# Revit family: Caroma TMV20 Bottom Inlet Hinged
name_source: partatom
category: Pipe Accessories
revit_build: Autodesk Revit LT 2014 (Build: 20130308_1515(x64)
units: mm (PartAtom-declared; Revit-internal decimal feet)

## types (2) — shared parameters
Assembly Code = D2090800
Description = Thermostatic Mixing Valve in Stainless Steel Enclosure (Hinged Door)
Height_ANZRS = 320 mm  [stored 1.04987 ft]
Length_ANZRS = 320 mm  [stored 1.04987 ft]
Manufacturer = GWA Bathrooms & Kitchens
Material_ANZRS = Metal-Stainless Steel-Brushed
ModifiedIssue_ANZRS = 20150421.04 $
PlumbingMaterial_ANZRS = Metal-Copper-Satin
Side2Flow_ANZRS = 0.7 L/s
Type Comments = Adjustable Temperature range 35-50°, Dynamic Working Pressure 20-500kPa, Maximum 1000kPa Inlet Pressure, Maximum Ratio 10:1
URL = http://specify.caroma.com.au
Width_ANZRS = 75 mm  [stored 0.246063 ft]
zero-valued in all types: K Coefficient

## per-type parameters (varying)
| type | Angle | End1 pos | End2 Pos | Model | Top Inlet |
| Bottom Inlet | 90.00° | 411 mm  [stored 1.34843 ft] | 522 mm | BTMV20-005 | No |
| Top Inlet | 270.00° | 111 mm | 0 mm  [stored 0 ft] | BTMV20-006 | Yes |

note: [stored X ft] marks values corroborated as IEEE doubles in the binary element streams (Revit-internal decimal feet)

## geometry (parser evidence)
native form markers: Sweep x1
no freeform markers — native parametric forms only
